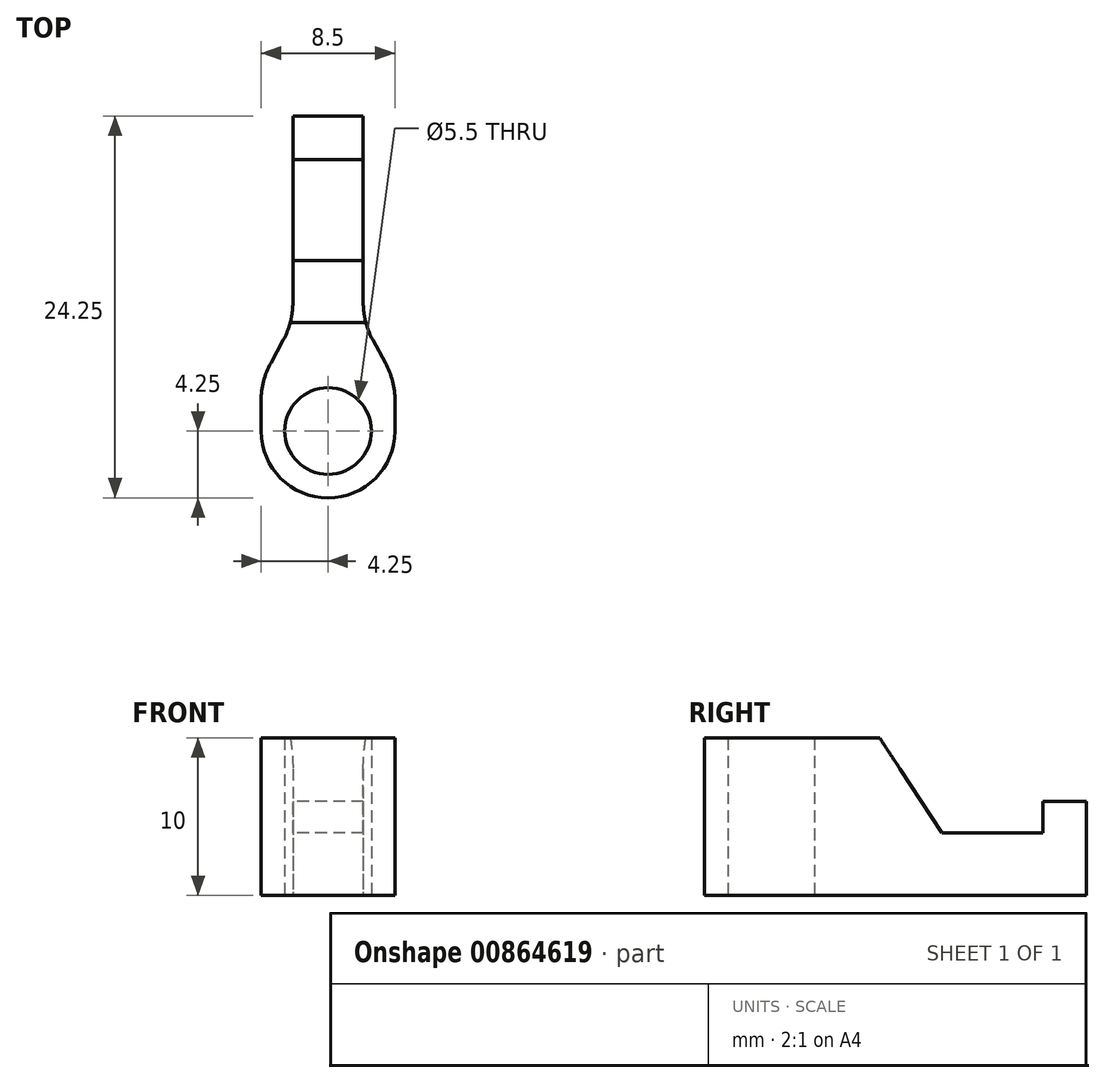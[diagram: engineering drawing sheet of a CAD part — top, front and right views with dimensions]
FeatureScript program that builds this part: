
annotation { "Feature Type Name" : "Feature", "Feature Type Description" : "" }
export const myFeature = defineFeature(function(context is Context, id is Id, definition is map)
    precondition{}
    {
        {
            var Q0;
            Q0=qCreatedBy(makeId("Top.planeOp"),FACE);
            var sketch = newSketch(context, id + "F0", { "sketchPlane" : qUnion([Q0])});
            skCircle(sketch, "E0", {"center": v(0, 0) * mm, "radius": 4.25 * mm});
            skLineSegment(sketch, "E1", {"start": v(-4.25, 0) * mm, "end": v(-4.25, 3.2) * mm});
            skLineSegment(sketch, "E2", {"start": v(4.25, 0) * mm, "end": v(4.25, 3.2) * mm});
            skLineSegment(sketch, "E3", {"start": v(-2.24, 20) * mm, "end": v(2.24, 20) * mm});
            skCircle(sketch, "E4", {"center": v(0, 0) * mm, "radius": 2.75 * mm});
            skLineSegment(sketch, "E5", {"start": v(-2.24, 10.9) * mm, "end": v(-2.24, 20) * mm});
            skLineSegment(sketch, "E6.MirrorCS", {"start": v(2.24, 10.9) * mm, "end": v(2.24, 20) * mm});
            skPoint(sketch, "E7.orphan", {"position": v(-4.25, 20) * mm});
            skLineSegment(sketch, "E8", {"start": v(2.24, 10.9) * mm, "end": v(2.24, 6.89) * mm});
            skLineSegment(sketch, "E9", {"start": v(2.24, 6.89) * mm, "end": v(4.25, 3.2) * mm});
            skPoint(sketch, "E10.MirrorCS.start.orphan", {"position": v(4.25, 7.97) * mm});
            skPoint(sketch, "E11.orphan", {"position": v(4.25, 20) * mm});
            skLineSegment(sketch, "E12.MirrorCS", {"start": v(-2.24, 6.89) * mm, "end": v(-4.25, 3.2) * mm});
            skLineSegment(sketch, "E13.MirrorCS", {"start": v(-2.24, 10.9) * mm, "end": v(-2.24, 6.89) * mm});
            skPoint(sketch, "E14.orphan", {"position": v(-4.25, 7.97) * mm});
            skSolve(sketch);
        }
        {
            var Q0;
            {var subQ0=sQuery(id+"F0.wireOp",EDGE,"E1");Q0=makeQuery(id+"F0.imprint","IMPRINT",FACE,{"disambiguationData":[TD([[makeQuery(id+"F0.imprint","IMPRINT",EDGE,{"derivedFrom":subQ0}),-1.0]])]});}
            var Q1;
            Q1=makeQuery(id+"F0.imprint","IMPRINT",FACE,{"disambiguationData":[TD([[makeQuery(id+"F0.imprint","IMPRINT",EDGE,{"derivedFrom":sQuery(id+"F0.wireOp",EDGE,"E4")}),-1.0]])]});
            extrude(context, id + "F1", {"entities" : qUnion([Q0, Q1]), "depth" : 10 * mm, "offsetDistance" : 25 * mm});
        }
        {
            var Q0;
            Q0=makeQuery(id+"F1.opExtrude","SWEPT_FACE",FACE,{"disambiguationData":[OSD([sQuery(id+"F0.wireOp",EDGE,"E5"),sQuery(id+"F0.wireOp",EDGE,"E13.MirrorCS")])]});
            var sketch = newSketch(context, id + "F2", { "sketchPlane" : qUnion([Q0])});
            skLineSegment(sketch, "E15", {"start": v(-6.89, 10) * mm, "end": v(-10.82, 3.98) * mm});
            skLineSegment(sketch, "E16", {"start": v(-10.82, 3.98) * mm, "end": v(-17.24, 3.98) * mm});
            skLineSegment(sketch, "E17", {"start": v(-17.24, 3.98) * mm, "end": v(-17.24, 5.96) * mm});
            skLineSegment(sketch, "E18", {"start": v(-17.24, 5.96) * mm, "end": v(-20, 5.96) * mm});
            skLineSegment(sketch, "E19", {"start": v(-20, 5.96) * mm, "end": v(-20, 10) * mm});
            skLineSegment(sketch, "E20", {"start": v(-20, 10) * mm, "end": v(-6.89, 10) * mm});
            skSolve(sketch);
        }
        {
            var Q0;
            Q0=makeQuery(id+"F2.imprint","IMPRINT",FACE,{"disambiguationData":[TD([[makeQuery(id+"F2.imprint","IMPRINT",EDGE,{"derivedFrom":sQuery(id+"F2.wireOp",EDGE,"E15")}),-1.0]])]});
            extrude(context, id + "F3", {"entities" : qUnion([Q0]), "operationType" : NewBodyOperationType.REMOVE, "oppositeDirection" : true, "depth" : 10 * mm, "offsetDistance" : 25 * mm});
        }
        {
            var Q0;
            Q0=makeQuery(id+"F1.opExtrude","SWEPT_EDGE",EDGE,{"disambiguationData":[OSD([sQuery(id+"F0.wireOp",EDGE,"E1"),sQuery(id+"F0.wireOp",EDGE,"E12.MirrorCS")])]});
            var Q1;
            Q1=makeQuery(id+"F1.opExtrude","SWEPT_EDGE",EDGE,{"disambiguationData":[OSD([sQuery(id+"F0.wireOp",EDGE,"E0"),sQuery(id+"F0.wireOp",EDGE,"E1")])]});
            var Q2;
            Q2=makeQuery(id+"F1.opExtrude","SWEPT_EDGE",EDGE,{"disambiguationData":[OSD([sQuery(id+"F0.wireOp",EDGE,"E12.MirrorCS"),sQuery(id+"F0.wireOp",EDGE,"E13.MirrorCS")])]});
            var Q3;
            Q3=makeQuery(id+"F1.opExtrude","SWEPT_EDGE",EDGE,{"disambiguationData":[OSD([sQuery(id+"F0.wireOp",EDGE,"E8"),sQuery(id+"F0.wireOp",EDGE,"E9")])]});
            var Q4;
            Q4=makeQuery(id+"F1.opExtrude","SWEPT_EDGE",EDGE,{"disambiguationData":[OSD([sQuery(id+"F0.wireOp",EDGE,"E2"),sQuery(id+"F0.wireOp",EDGE,"E9")])]});
            var Q5;
            Q5=makeQuery(id+"F1.opExtrude","SWEPT_EDGE",EDGE,{"disambiguationData":[OSD([sQuery(id+"F0.wireOp",EDGE,"E0"),sQuery(id+"F0.wireOp",EDGE,"E2")])]});
            fillet(context, id + "F4", {"entities" : qUnion([Q0, Q1, Q2, Q3, Q4, Q5]), "radius" : 5 * mm, "tangentPropagation" : true, "allowEdgeOverflow" : false});
        }
    });
